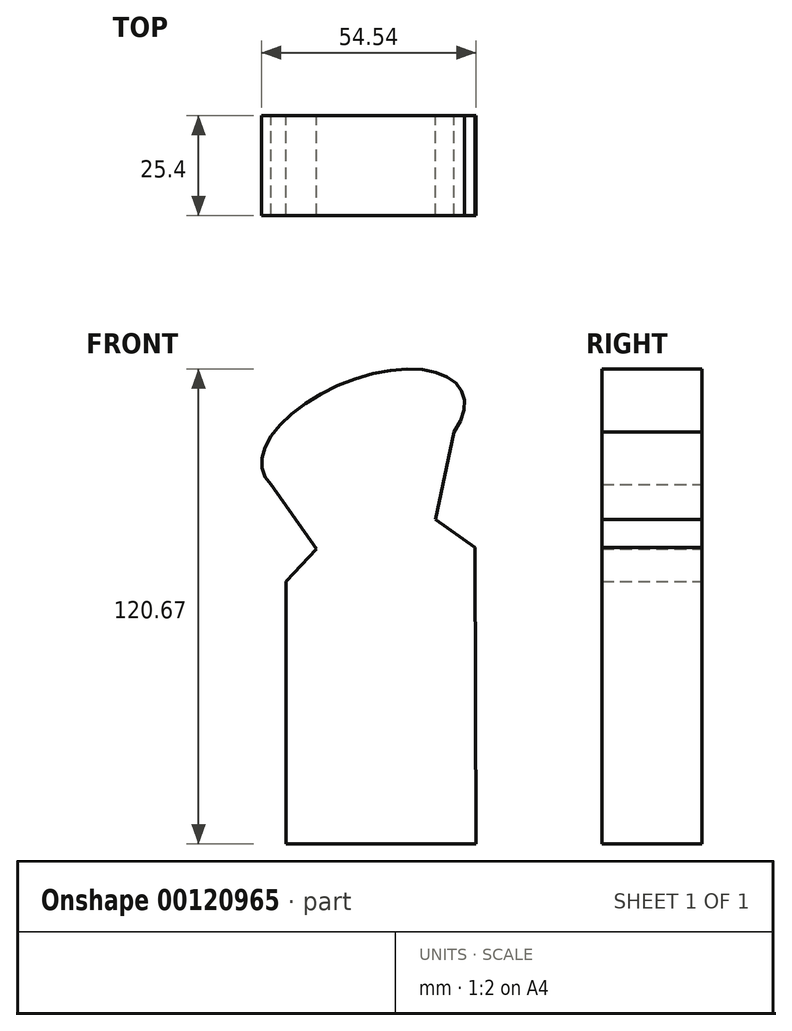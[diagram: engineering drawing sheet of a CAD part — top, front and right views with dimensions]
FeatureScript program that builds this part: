
annotation { "Feature Type Name" : "Feature", "Feature Type Description" : "" }
export const myFeature = defineFeature(function(context is Context, id is Id, definition is map)
    precondition{}
    {
        {
            var Q0;
            Q0=qCreatedBy(makeId("Front.planeOp"),FACE);
            var sketch = newSketch(context, id + "F0", { "sketchPlane" : qUnion([Q0])});
            skEllipse(sketch, "E0", {"center": v(11.78, 52.43) * mm, "majorRadius": 27.32 * mm, "minorRadius": 13.73 * mm, "majorAxis": v(-0.93, -0.38)});
            skLineSegment(sketch, "E1", {"start": v(-13.5, 42.09) * mm, "end": v(0, 23.13) * mm});
            skLineSegment(sketch, "E2", {"start": v(0, 23.13) * mm, "end": v(-7.76, 14.8) * mm});
            skLineSegment(sketch, "E3", {"start": v(-7.76, 14.8) * mm, "end": v(-7.76, -51.86) * mm});
            skLineSegment(sketch, "E4", {"start": v(-7.76, -51.86) * mm, "end": v(40.5, -51.86) * mm});
            skPoint(sketch, "E5.endSnap0", {"position": v(37.06, 62.77) * mm});
            skLineSegment(sketch, "E6", {"start": v(37.06, 62.77) * mm, "end": v(30.17, 30.6) * mm});
            skLineSegment(sketch, "E7", {"start": v(30.17, 30.6) * mm, "end": v(40.22, 23.41) * mm});
            skLineSegment(sketch, "E8", {"start": v(40.22, 23.41) * mm, "end": v(40.5, -51.86) * mm});
            skSolve(sketch);
        }
        {
            var Q0;
            Q0 = qSketchRegion(id + "F0", true);
            extrude(context, id + "F1", {"entities" : qUnion([Q0]), "depth" : 25.4 * mm});
        }
    });
